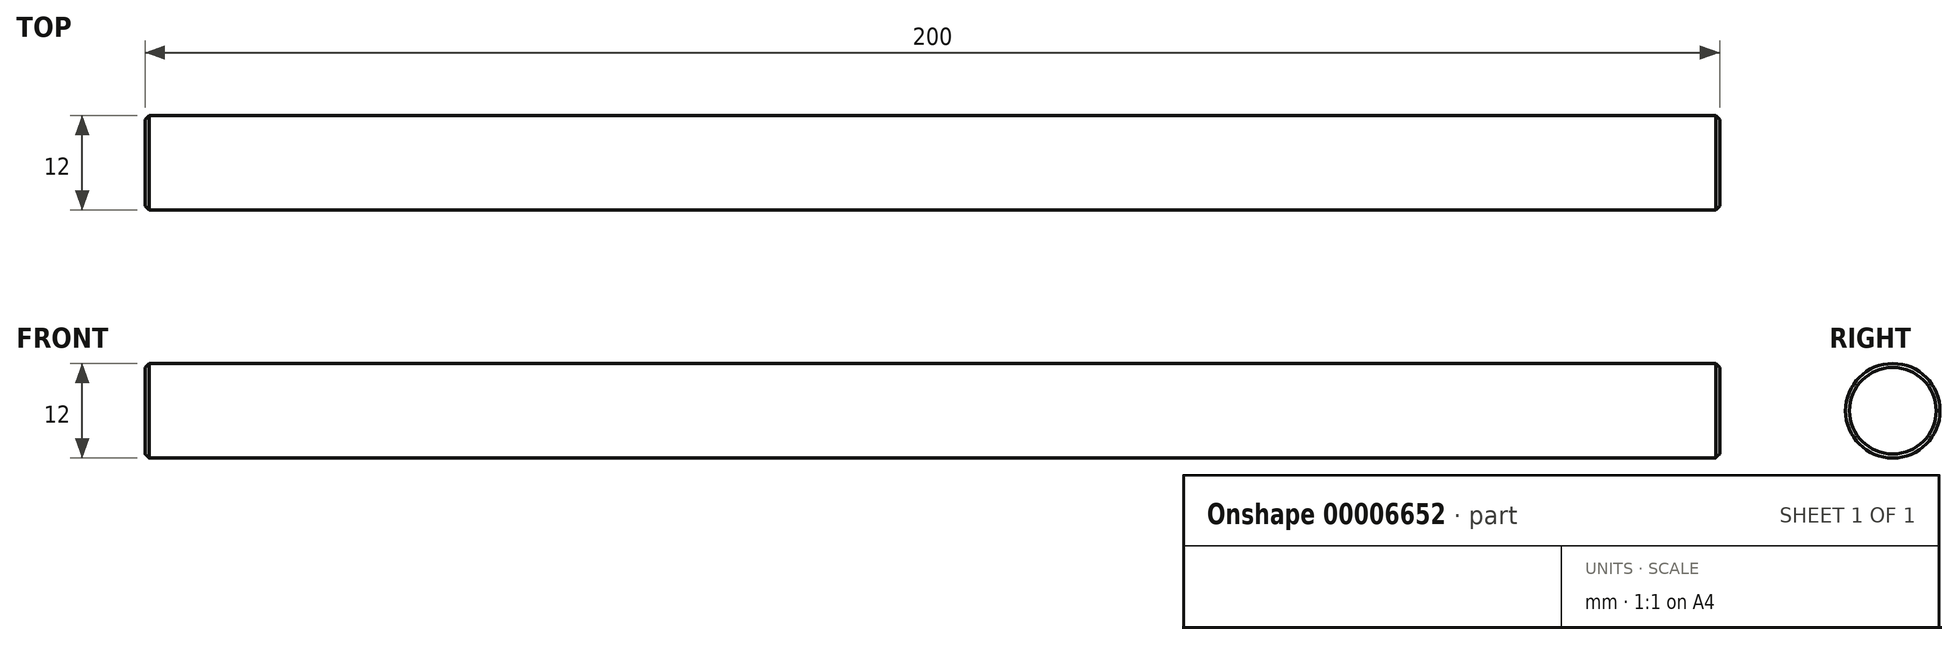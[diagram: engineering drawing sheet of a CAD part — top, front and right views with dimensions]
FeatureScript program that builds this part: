
annotation { "Feature Type Name" : "Feature", "Feature Type Description" : "" }
export const myFeature = defineFeature(function(context is Context, id is Id, definition is map)
    precondition{}
    {
        {
            var Q0;
            Q0=qCreatedBy(makeId("Right.planeOp"),FACE);
            var sketch = newSketch(context, id + "F0", { "sketchPlane" : qUnion([Q0])});
            skCircle(sketch, "E0", {"center": v(0, 0) * mm, "radius": 6 * mm});
            skSolve(sketch);
        }
        {
            var Q0;
            Q0 = qSketchRegion(id + "F0", true);
            extrude(context, id + "F1", {"entities" : qUnion([Q0]), "depth" : 200 * mm});
        }
        {
            var Q0;
            Q0=makeQuery(id+"F1.opExtrude","CAP_EDGE",EDGE,{"disambiguationData":[OSD([sQuery(id+"F0.wireOp",EDGE,"E0")])],"isStart":true});
            var Q1;
            Q1=makeQuery(id+"F1.opExtrude","CAP_EDGE",EDGE,{"disambiguationData":[OSD([sQuery(id+"F0.wireOp",EDGE,"E0")])],"isStart":false});
            chamfer(context, id + "F2", {"entities" : qUnion([Q0, Q1]), "width" : .5 * mm, "tangentPropagation" : true});
        }
    });
